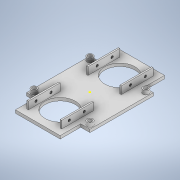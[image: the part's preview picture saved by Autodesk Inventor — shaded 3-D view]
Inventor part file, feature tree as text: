
AUTODESK INVENTOR PART (.ipt)
format: ipt  version: 2020 (Build 240168000, 168)  size: 2,649,600 bytes
history: native  units: mm
features: sketch x23, thread x8, revolve x8, helix x8, extrude x5
ambient origin geometry x8: Origin, YZ Plane, XZ Plane, XY Plane, X Axis, Y Axis, Z Axis, Center Point
bodies: Solid1 (feature_tree), Solid8 (feature_tree), Solid9 (feature_tree), Solid12 (feature_tree), Solid13 (feature_tree), Solid14 (feature_tree), Solid15 (feature_tree), Solid16 (feature_tree), Solid17 (feature_tree)
feature tree (52):
  extrude  "Extrusion1"  Depth=85.0mm
  extrude  "Extrusion2"  Depth=75.0mm
  sketch  "Sketch18"  dims[d4=5.2mm d5=72.0mm d6=72.0mm d7=20.0mm d9=75.0mm d10=20.0mm d12=75.0mm d15=4.0mm d16=0.0mm d28=10.0mm d29=0.0mm d63=9.599311mm d81=9.599311mm d99=9.599311mm d117=9.599311mm]
  extrude  "Extrusion6"  Depth=10.0mm
  thread  "Thread7"  [1 undecoded]
  thread  "Thread8"  [1 undecoded]
  thread  "Thread11"  [1 undecoded]
  thread  "Thread12"  [1 undecoded]
  thread  "Thread13"  [1 undecoded]
  thread  "Thread14"  [1 undecoded]
  thread  "Thread15"  [1 undecoded]
  thread  "Thread16"  [1 undecoded]
  revolve  "Revolution7"  [1 undecoded]
  helix  "Coil7"  [1 undecoded]
  revolve  "Revolution8"  [1 undecoded]
  helix  "Coil8"  [1 undecoded]
  revolve  "Revolution11"  [1 undecoded]
  helix  "Coil11"  [1 undecoded]
  revolve  "Revolution12"  [1 undecoded]
  helix  "Coil12"  [1 undecoded]
  revolve  "Revolution13"  [1 undecoded]
  helix  "Coil13"  [1 undecoded]
  revolve  "Revolution14"  [1 undecoded]
  helix  "Coil14"  [1 undecoded]
  revolve  "Revolution15"  [1 undecoded]
  helix  "Coil15"  [1 undecoded]
  revolve  "Revolution16"  [1 undecoded]
  helix  "Coil16"  [1 undecoded]
  sketch  "Sketch43"  dims[d324=0.0mm]
  sketch  "Sketch44"  dims[d325=0.5005mm d326=3.0mm d327=10.0mm d328=0.0mm d329=0.0mm d330=0.0mm d331=0.0mm d332=0.0mm]
  extrude  "Extrusion7"  Depth=0.5mm
  extrude  "Extrusion8"  TaperAngle=0.0deg  [1 undecoded]
  sketch  "Sketch1"  dims[d0=85.0mm d1=85.0mm]
  sketch  "Sketch2"  dims[d2=75.0mm d3=75.0mm]
  sketch  "Sketch19"  dims[d135=9.599311mm d153=9.599311mm d164=60.0mm]
  sketch  "Sketch20"  dims[d165=30.0mm d167=20.0mm d169=20.0mm d170=60.0mm d171=30.0mm d172=40.5mm]
  sketch  "Sketch21"  dims[d173=40.5mm]
  sketch  "Sketch22"  dims[d176=42.6mm d177=42.6mm d178=42.6mm d179=2.0mm d180=44.6mm d181=46.6mm d191=20.0mm d192=3.3mm]
  sketch  "Sketch27"  dims[d193=3.3mm d194=20.0mm d195=3.3mm d196=3.3mm d199=0.0mm d200=0.0mm]
  sketch  "Sketch28"  dims[d201=2.0mm d202=0.0mm d203=2.0mm d204=0.0mm d209=2.0mm d210=0.0mm d211=2.0mm d212=0.0mm d213=2.0mm d214=0.0mm d215=2.0mm d216=0.0mm d217=2.0mm d218=0.0mm d219=2.0mm d220=0.0mm d225=9.599311mm d226=0.080042mm d227=0.080042mm d230=0.5mm]
  sketch  "Sketch29"  dims[d232=9.599311mm d234=0.0mm]
  sketch  "Sketch30"  dims[d235=0.5005mm d236=3.0mm d237=10.0mm d238=0.0mm d239=0.0mm d240=0.0mm d241=0.0mm d242=0.0mm d243=9.599311mm d244=0.080042mm d245=0.080042mm]
  sketch  "Sketch31"  dims[d248=0.5mm d250=9.599311mm d252=0.0mm]
  sketch  "Sketch32"  dims[d253=0.5005mm d254=3.0mm d255=10.0mm d256=0.0mm d257=0.0mm d258=0.0mm d259=0.0mm d260=0.0mm d268=9.599311mm d286=9.599311mm]
  sketch  "Sketch33"  dims[d297=9.599311mm d298=0.080042mm d299=0.080042mm d302=0.5mm]
  sketch  "Sketch34"  dims[d304=9.599311mm d306=0.0mm]
  sketch  "Sketch35"  dims[d307=0.5005mm d308=3.0mm d309=10.0mm d310=0.0mm d311=0.0mm d312=0.0mm d313=0.0mm d314=0.0mm]
  sketch  "Sketch36"  dims[d315=9.599311mm d316=0.080042mm d317=0.080042mm]
  sketch  "Sketch37"  dims[d320=0.5mm]
  sketch  "Sketch38"  dims[d322=9.599311mm]
  sketch  "Sketch45"  dims[d333=9.599311mm d334=0.080042mm d335=0.080042mm]
  sketch  "Sketch46"  dims[d338=0.5mm d340=9.599311mm d342=0.0mm d343=0.5005mm d344=3.0mm d345=10.0mm d346=0.0mm d347=0.0mm d348=0.0mm d349=0.0mm d350=0.0mm d351=9.599311mm d352=0.080042mm d353=0.080042mm d356=0.5mm d358=9.599311mm d360=0.0mm d361=0.5005mm d362=3.0mm d363=10.0mm d364=0.0mm d365=0.0mm d366=0.0mm d367=0.0mm d368=0.0mm d369=9.599311mm d370=0.080042mm d371=0.080042mm d374=0.5mm d376=9.599311mm d378=0.0mm d379=0.5005mm d380=3.0mm d381=10.0mm d382=0.0mm d383=0.0mm d384=0.0mm d385=0.0mm d386=0.0mm d387=9.599311mm d388=0.080042mm d389=0.080042mm d392=0.5mm d394=9.599311mm d396=0.0mm d397=0.5005mm d398=3.0mm d399=10.0mm d400=0.0mm d401=0.0mm d402=0.0mm d403=0.0mm d404=0.0mm d412=9.599311mm d430=9.599311mm d441=2.5mm d442=2.5mm d443=75.0mm d444=75.0mm d445=5.2mm d446=20.0mm d448=75.0mm d449=20.0mm d451=75.0mm d454=2.0mm d455=0.0mm d456=8.0mm d457=75.0mm d458=75.0mm d459=20.0mm d461=75.0mm d462=20.0mm d464=75.0mm d467=5.0mm d468=0.0mm d469=0.5mm d470=0.872665mm]
note: 25 required parameter values undecoded (feature->parameter linkage not recoverable at this tier; creation-order binding heuristic only, values carry confidence <= 0.55)